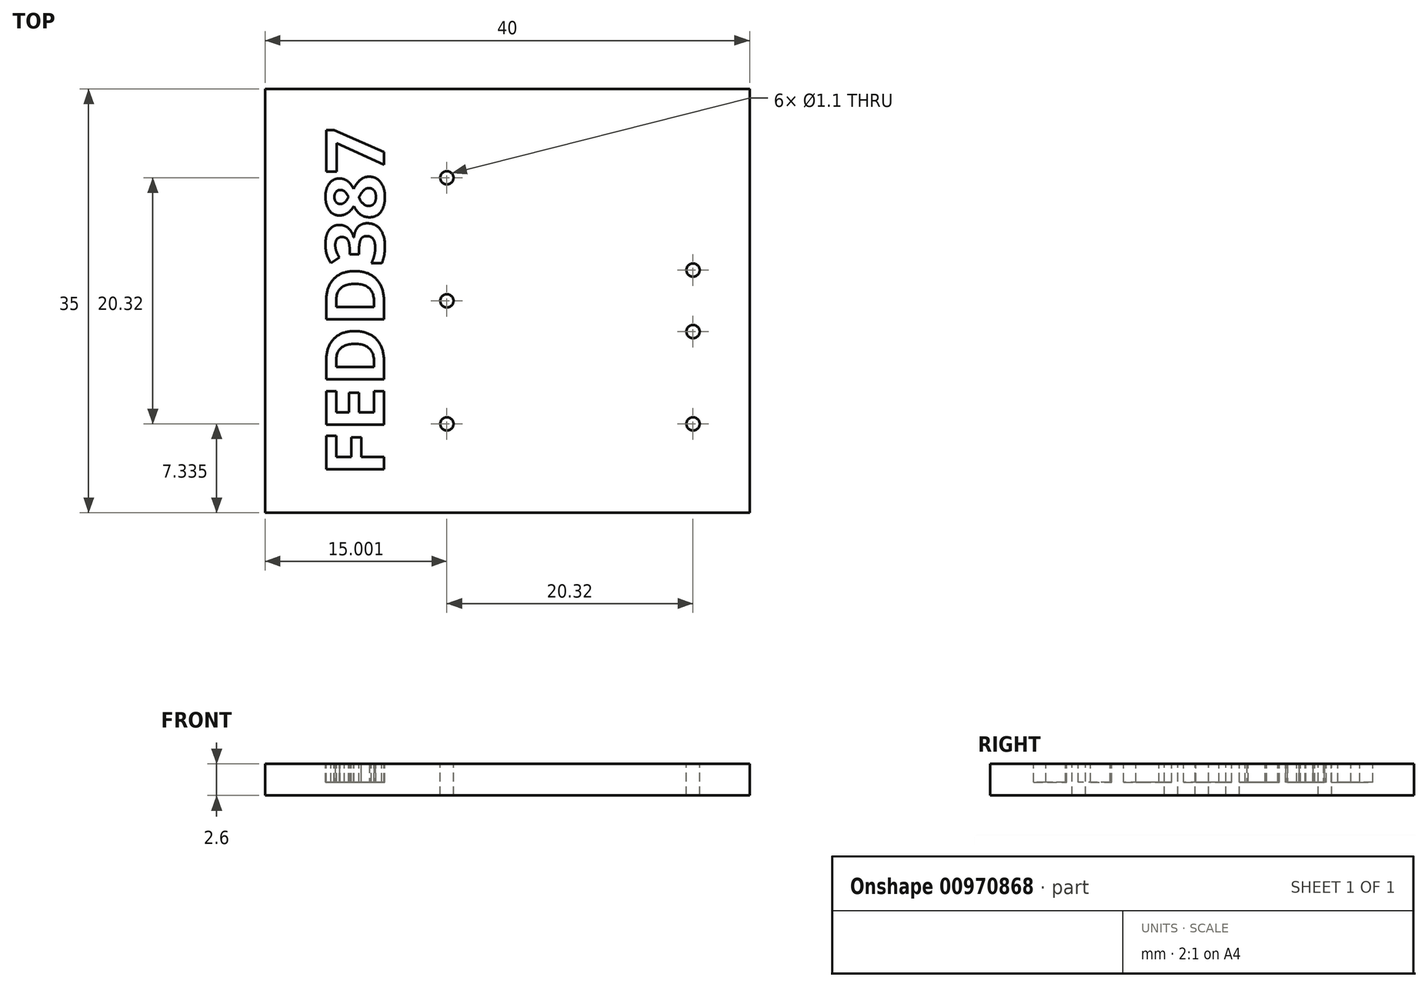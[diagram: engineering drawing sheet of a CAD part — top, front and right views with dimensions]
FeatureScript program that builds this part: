
annotation { "Feature Type Name" : "Feature", "Feature Type Description" : "" }
export const myFeature = defineFeature(function(context is Context, id is Id, definition is map)
    precondition{}
    {
        {
            var Q0;
            Q0=qCreatedBy(makeId("Top.planeOp"),FACE);
            var sketch = newSketch(context, id + "F0", { "sketchPlane" : qUnion([Q0])});
            skLineSegment(sketch, "E0.bottom", {"start": v(-43.16, 13.34) * mm, "end": v(-3.16, 13.34) * mm});
            skLineSegment(sketch, "E0.top", {"start": v(-43.16, -21.66) * mm, "end": v(-3.16, -21.66) * mm});
            skLineSegment(sketch, "E0.left", {"start": v(-43.16, 13.34) * mm, "end": v(-43.16, -21.66) * mm});
            skLineSegment(sketch, "E0.right", {"start": v(-3.16, 13.34) * mm, "end": v(-3.16, -21.66) * mm});
            skSolve(sketch);
        }
        {
            var Q0;
            Q0=makeQuery(id+"F0.imprint","IMPRINT",FACE,{"disambiguationData":[TD([[makeQuery(id+"F0.imprint","IMPRINT",EDGE,{"derivedFrom":sQuery(id+"F0.wireOp",EDGE,"E0.bottom")}),-1.0]])]});
            extrude(context, id + "F1", {"entities" : qUnion([Q0]), "depth" : 2.6 * mm, "offsetDistance" : 25 * mm});
        }
        {
            var Q0;
            Q0=makeQuery(id+"F1.opExtrude","CAP_FACE",FACE,{"disambiguationData":[OSD([sQuery(id+"F0.wireOp",EDGE,"E0.bottom"),sQuery(id+"F0.wireOp",EDGE,"E0.top"),sQuery(id+"F0.wireOp",EDGE,"E0.left"),sQuery(id+"F0.wireOp",EDGE,"E0.right")])],"isStart":false});
            var sketch = newSketch(context, id + "F2", { "sketchPlane" : qUnion([Q0])});
            skText(sketch, "E1", { "text": "FEDD387", "fontName": "OpenSans-Bold.ttf"});
            const initialGuessF2  = {"E1": [-0.03334, -0.01866, 0, 1, 0.00482]};
            skSetInitialGuess(sketch, initialGuessF2);
            skSolve(sketch);
        }
        {
            var Q0;
            Q0=qSketchRegion(id+"F2",true);
            extrude(context, id + "F3", {"entities" : qUnion([Q0]), "operationType" : NewBodyOperationType.REMOVE, "oppositeDirection" : true, "depth" : 1.5 * mm, "offsetDistance" : 25 * mm});
        }
        {
            var Q0;
            {var subQ0=sQuery(id+"F0.wireOp",EDGE,"E0.left");var subQ1=sQuery(id+"F0.wireOp",EDGE,"E0.bottom");var subQ2=sQuery(id+"F0.wireOp",EDGE,"E0.right");var subQ3=sQuery(id+"F0.wireOp",EDGE,"E0.top");Q0=makeQuery(id+"F3.boolean.opBoolean","SPLIT",FACE,{"disambiguationData":[TD([makeQuery(id+"F1.opExtrude","SWEPT_FACE",FACE,{"disambiguationData":[OSD([subQ1])]})])],"derivedFrom":makeQuery(id+"F1.opExtrude","CAP_FACE",FACE,{"disambiguationData":[OSD([subQ1,subQ3,subQ0,subQ2])],"isStart":false})});}
            var sketch = newSketch(context, id + "F4", { "sketchPlane" : qUnion([Q0])});
            skCircle(sketch, "E2", {"center": v(-28.16, 6) * mm, "radius": 0.55 * mm});
            skCircle(sketch, "E3", {"center": v(-28.16, -4.16) * mm, "radius": 0.55 * mm});
            skCircle(sketch, "E4", {"center": v(-28.16, -14.32) * mm, "radius": 0.55 * mm});
            skCircle(sketch, "E5", {"center": v(-7.84, -1.62) * mm, "radius": 0.55 * mm});
            skCircle(sketch, "E6", {"center": v(-7.84, -6.7) * mm, "radius": 0.55 * mm});
            skCircle(sketch, "E7", {"center": v(-7.84, -14.32) * mm, "radius": 0.55 * mm});
            skSolve(sketch);
        }
        {
            var Q0;
            Q0 = qSketchRegion(id + "F4", true);
            extrude(context, id + "F5", {"entities" : qUnion([Q0]), "operationType" : NewBodyOperationType.REMOVE, "endBound" : BoundingType.UP_TO_NEXT, "oppositeDirection" : true, "depth" : 25 * mm, "offsetDistance" : 25 * mm});
        }
    });
